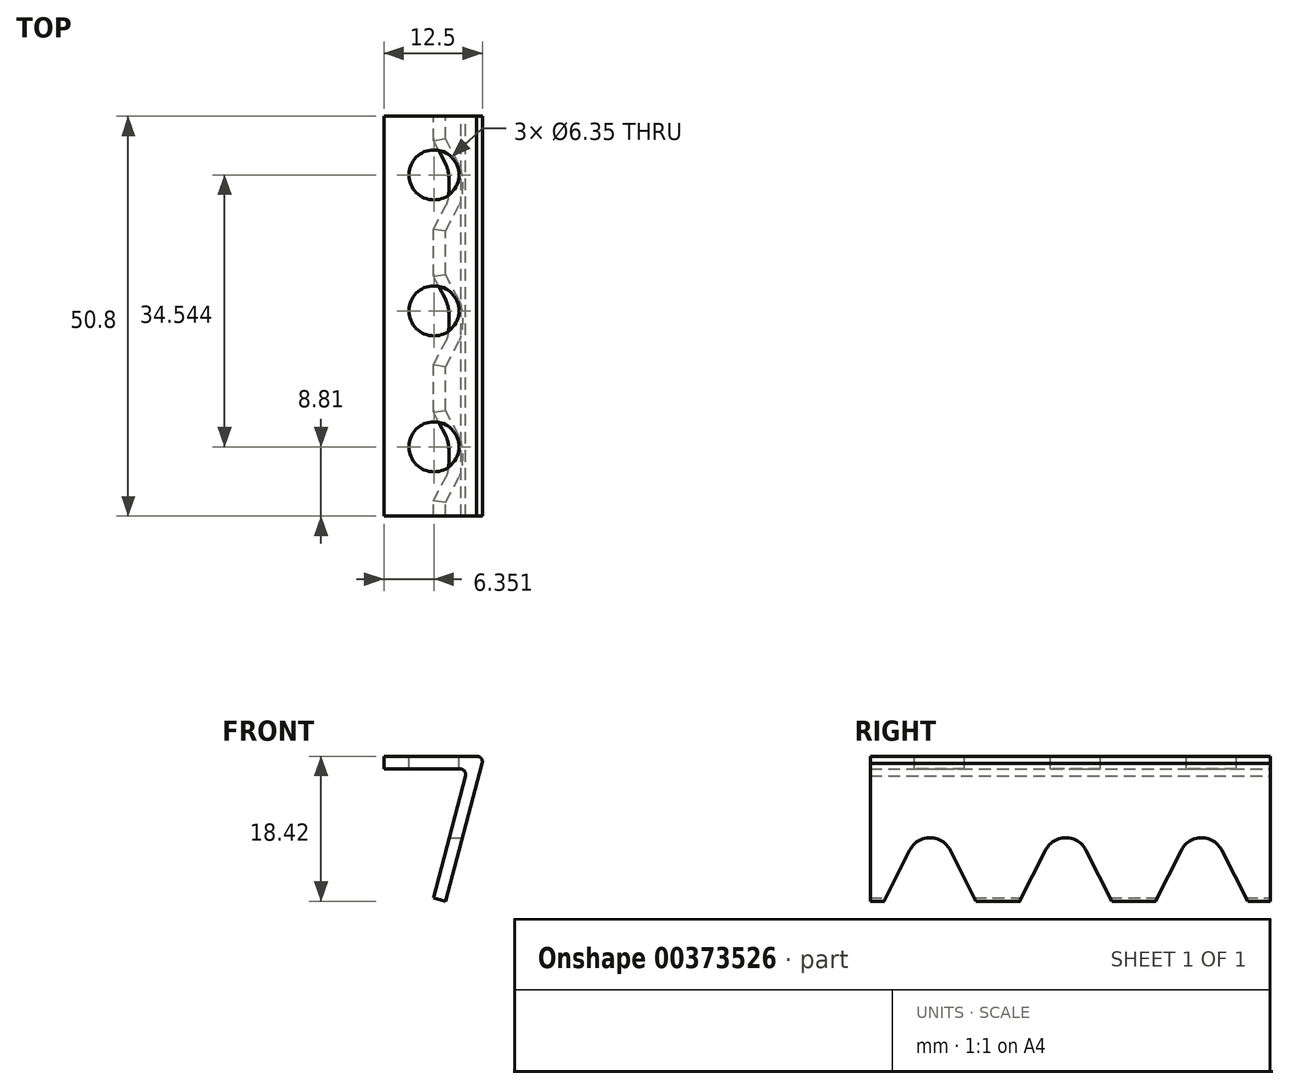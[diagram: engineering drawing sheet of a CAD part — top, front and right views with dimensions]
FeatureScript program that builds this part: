
annotation { "Feature Type Name" : "Feature", "Feature Type Description" : "" }
export const myFeature = defineFeature(function(context is Context, id is Id, definition is map)
    precondition{}
    {
        {
            var Q0;
            Q0=qCreatedBy(makeId("Front.planeOp"),FACE);
            var sketch = newSketch(context, id + "F0", { "sketchPlane" : qUnion([Q0])});
            skLineSegment(sketch, "E0", {"start": v(-9.49, 8.56) * mm, "end": v(2.38, 8.56) * mm});
            skLineSegment(sketch, "E1", {"start": v(3, 7.74) * mm, "end": v(-1.67, -9.85) * mm});
            skLineSegment(sketch, "E2.0", {"start": v(-9.49, 6.95) * mm, "end": v(0.29, 6.95) * mm});
            skLineSegment(sketch, "E3", {"start": v(-3.23, -9.44) * mm, "end": v(-1.67, -9.85) * mm});
            skLineSegment(sketch, "E4", {"start": v(-9.49, 8.56) * mm, "end": v(-9.49, 6.95) * mm});
            skLineSegment(sketch, "E5.trimOffspring", {"start": v(0.88, 6.08) * mm, "end": v(-3.23, -9.44) * mm});
            skArc(sketch, "E6", {"start": v(0.88, 6.08) * mm, "mid": v(0.67, 6.75) * mm, "end": v(0, 6.95) * mm});
            skArc(sketch, "E7", {"start": v(2.98, 7.67) * mm, "mid": v(2.86, 8.3) * mm, "end": v(2.28, 8.56) * mm});
            skSolve(sketch);
        }
        {
            var Q0;
            Q0 = qSketchRegion(id + "F0", true);
            extrude(context, id + "F1", {"entities" : qUnion([Q0]), "depth" : 50.8 * mm});
        }
        {
            var Q0;
            Q0=qCreatedBy(makeId("Right.planeOp"),FACE);
            var sketch = newSketch(context, id + "F2", { "sketchPlane" : qUnion([Q0])});
            skLineSegment(sketch, "E8", {"start": v(-49.07, -9.85) * mm, "end": v(-45.8, -3.38) * mm});
            skArc(sketch, "E9", {"start": v(-40.62, -3.38) * mm, "mid": v(-43.21, -1.8) * mm, "end": v(-45.8, -3.38) * mm});
            skLineSegment(sketch, "E10", {"start": v(-40.62, -3.38) * mm, "end": v(-37.29, -9.97) * mm});
            skLineSegment(sketch, "E11", {"start": v(-37.29, -9.97) * mm, "end": v(-49.07, -9.85) * mm});
            skArc(sketch, "E12.1.0.0", {"start": v(-23.38, -3.38) * mm, "mid": v(-25.96, -1.8) * mm, "end": v(-28.55, -3.38) * mm});
            skLineSegment(sketch, "E12.1.0.1", {"start": v(-31.83, -9.85) * mm, "end": v(-28.55, -3.38) * mm});
            skLineSegment(sketch, "E12.1.0.2", {"start": v(-20.04, -9.97) * mm, "end": v(-31.83, -9.85) * mm});
            skArc(sketch, "E12.2.0.0", {"start": v(-6.13, -3.38) * mm, "mid": v(-8.72, -1.8) * mm, "end": v(-11.3, -3.38) * mm});
            skLineSegment(sketch, "E12.2.0.1", {"start": v(-14.58, -9.85) * mm, "end": v(-11.3, -3.38) * mm});
            skLineSegment(sketch, "E12.2.0.2", {"start": v(-2.8, -9.97) * mm, "end": v(-14.58, -9.85) * mm});
            skLineSegment(sketch, "E12.direction1", {"start": v(-49.07, -9.85) * mm, "end": v(-31.83, -9.85) * mm, "construction": true});
            skLineSegment(sketch, "E13", {"start": v(-23.38, -3.38) * mm, "end": v(-20.04, -9.97) * mm});
            skLineSegment(sketch, "E14", {"start": v(-6.13, -3.38) * mm, "end": v(-2.8, -9.97) * mm});
            skSolve(sketch);
        }
        {
            var Q0;
            Q0 = qSketchRegion(id + "F2", true);
            extrude(context, id + "F3", {"entities" : qUnion([Q0]), "operationType" : NewBodyOperationType.REMOVE, "oppositeDirection" : true, "depth" : 25.4 * mm, "hasSecondDirection" : true, "secondDirectionOppositeDirection" : false, "secondDirectionDepth" : 25.4 * mm});
        }
        {
            var Q0;
            Q0=makeQuery(id+"F1.opExtrude","SWEPT_FACE",FACE,{"disambiguationData":[OSD([sQuery(id+"F0.wireOp",EDGE,"E0")])]});
            var sketch = newSketch(context, id + "F4", { "sketchPlane" : qUnion([Q0])});
            skCircle(sketch, "E15", {"center": v(-3.14, -7.45) * mm, "radius": 3.18 * mm});
            skCircle(sketch, "E16.0.1.0", {"center": v(-3.14, -24.72) * mm, "radius": 3.18 * mm});
            skCircle(sketch, "E16.0.2.0", {"center": v(-3.14, -41.99) * mm, "radius": 3.18 * mm});
            skLineSegment(sketch, "E16.direction1", {"start": v(-3.14, -7.45) * mm, "end": v(22.26, -7.45) * mm, "construction": true});
            skLineSegment(sketch, "E16.direction2", {"start": v(-3.14, -7.45) * mm, "end": v(-3.14, -24.72) * mm, "construction": true});
            skSolve(sketch);
        }
        {
            var Q0;
            Q0 = qSketchRegion(id + "F4", true);
            var Q1;
            Q1=makeQuery(id+"F1.opExtrude","SWEPT_FACE",FACE,{"disambiguationData":[OSD([sQuery(id+"F0.wireOp",EDGE,"E2.0")])]});
            extrude(context, id + "F5", {"entities" : qUnion([Q0]), "operationType" : NewBodyOperationType.REMOVE, "endBound" : BoundingType.UP_TO_SURFACE, "oppositeDirection" : true, "endBoundEntityFace" : qUnion([Q1]), "depth" : 25.4 * mm});
        }
    });
